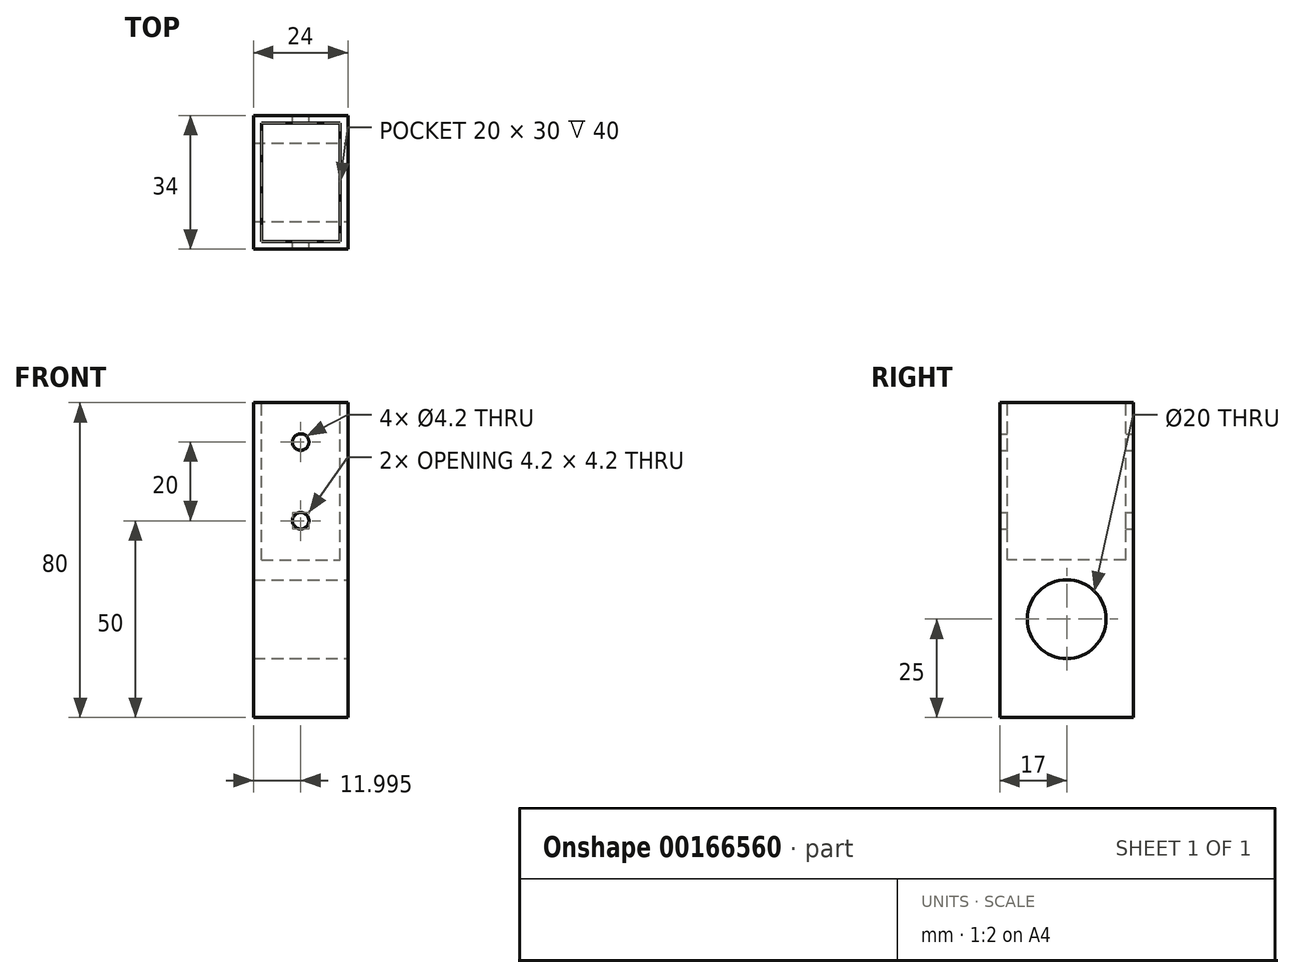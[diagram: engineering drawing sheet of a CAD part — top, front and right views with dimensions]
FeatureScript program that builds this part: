
annotation { "Feature Type Name" : "Feature", "Feature Type Description" : "" }
export const myFeature = defineFeature(function(context is Context, id is Id, definition is map)
    precondition{}
    {
        {
            var Q0;
            Q0=qCreatedBy(makeId("Top.planeOp"),FACE);
            var sketch = newSketch(context, id + "F0", { "sketchPlane" : qUnion([Q0])});
            skLineSegment(sketch, "E0.bottom", {"start": v(-30.13, 34) * mm, "end": v(-6.13, 34) * mm});
            skLineSegment(sketch, "E0.top", {"start": v(-30.13, 0) * mm, "end": v(-6.13, 0) * mm});
            skLineSegment(sketch, "E0.left", {"start": v(-30.13, 34) * mm, "end": v(-30.13, 0) * mm});
            skLineSegment(sketch, "E0.right", {"start": v(-6.13, 34) * mm, "end": v(-6.13, 0) * mm});
            skSolve(sketch);
        }
        {
            var Q0;
            Q0 = qSketchRegion(id + "F0", true);
            extrude(context, id + "F1", {"entities" : qUnion([Q0]), "depth" : 80 * mm});
        }
        {
            var Q0;
            Q0=makeQuery(id+"F1.opExtrude","SWEPT_FACE",FACE,{"disambiguationData":[OSD([sQuery(id+"F0.wireOp",EDGE,"E0.right")])]});
            var sketch = newSketch(context, id + "F2", { "sketchPlane" : qUnion([Q0])});
            skCircle(sketch, "E1", {"center": v(17, 25) * mm, "radius": 10 * mm});
            skSolve(sketch);
        }
        {
            var Q0;
            Q0=makeQuery(id+"F2.imprint","IMPRINT",FACE,{"disambiguationData":[TD([[makeQuery(id+"F2.imprint","IMPRINT",EDGE,{"derivedFrom":sQuery(id+"F2.wireOp",EDGE,"E1")}),1.0]])]});
            extrude(context, id + "F3", {"entities" : qUnion([Q0]), "operationType" : NewBodyOperationType.REMOVE, "oppositeDirection" : true, "depth" : 25 * mm});
        }
        {
            var Q0;
            Q0=makeQuery(id+"F1.opExtrude","CAP_FACE",FACE,{"disambiguationData":[OSD([sQuery(id+"F0.wireOp",EDGE,"E0.bottom"),sQuery(id+"F0.wireOp",EDGE,"E0.top"),sQuery(id+"F0.wireOp",EDGE,"E0.left"),sQuery(id+"F0.wireOp",EDGE,"E0.right")])],"isStart":false});
            var sketch = newSketch(context, id + "F4", { "sketchPlane" : qUnion([Q0])});
            skLineSegment(sketch, "E2.bottom", {"start": v(-28.13, 32) * mm, "end": v(-8.13, 32) * mm});
            skLineSegment(sketch, "E2.top", {"start": v(-28.13, 2) * mm, "end": v(-8.13, 2) * mm});
            skLineSegment(sketch, "E2.left", {"start": v(-28.13, 32) * mm, "end": v(-28.13, 2) * mm});
            skLineSegment(sketch, "E2.right", {"start": v(-8.13, 32) * mm, "end": v(-8.13, 2) * mm});
            skSolve(sketch);
        }
        {
            var Q0;
            Q0 = qSketchRegion(id + "F4", true);
            extrude(context, id + "F5", {"entities" : qUnion([Q0]), "operationType" : NewBodyOperationType.REMOVE, "oppositeDirection" : true, "depth" : 40 * mm});
        }
        {
            var Q0;
            Q0=makeQuery(id+"F1.opExtrude","SWEPT_FACE",FACE,{"disambiguationData":[OSD([sQuery(id+"F0.wireOp",EDGE,"E0.bottom")])]});
            var sketch = newSketch(context, id + "F6", { "sketchPlane" : qUnion([Q0])});
            skCircle(sketch, "E3", {"center": v(18.13, 70) * mm, "radius": 2.1 * mm});
            skCircle(sketch, "E4", {"center": v(18.13, 50) * mm, "radius": 2.1 * mm});
            skSolve(sketch);
        }
        {
            var Q0;
            Q0 = qSketchRegion(id + "F6", true);
            extrude(context, id + "F7", {"entities" : qUnion([Q0]), "operationType" : NewBodyOperationType.REMOVE, "oppositeDirection" : true, "depth" : 40 * mm});
        }
    });
